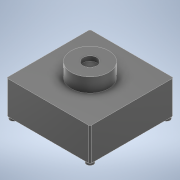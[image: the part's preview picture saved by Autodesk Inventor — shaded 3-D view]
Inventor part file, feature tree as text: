
AUTODESK INVENTOR PART (.ipt)
format: ipt  version: 2021 (Build 250183000, 183)  size: 144,896 bytes
history: native  units: mm
features: extrude x4, sketch x4, fillet x1
ambient origin geometry x8: Origin, YZ Plane, XZ Plane, XY Plane, X Axis, Y Axis, Z Axis, Center Point
bodies: Solid1 (feature_tree)
feature tree (9):
  extrude  "Extrusion1"  Depth=178.0mm
  extrude  "Extrusion2"  Depth=178.0mm
  extrude  "Extrusion3"  Depth=70.0mm
  extrude  "Extrusion4"  Depth=30.0mm
  fillet  "Fillet1"  Radius=10.0mm
  sketch  "Sketch1"  dims[d0=89.0mm d1=178.0mm]
  sketch  "Sketch2"  dims[d2=178.0mm d3=89.0mm]
  sketch  "Sketch3"  dims[d4=70.0mm d5=0.0mm d6=80.0mm]
  sketch  "Sketch4"  dims[d7=30.0mm d8=0.0mm d9=30.0mm d10=10.0mm d11=0.0mm d12=15.0mm d13=7.5mm d14=7.5mm d15=40.0mm d17=360.0deg d19=5.0mm d20=0.0mm d21=3.0mm]
